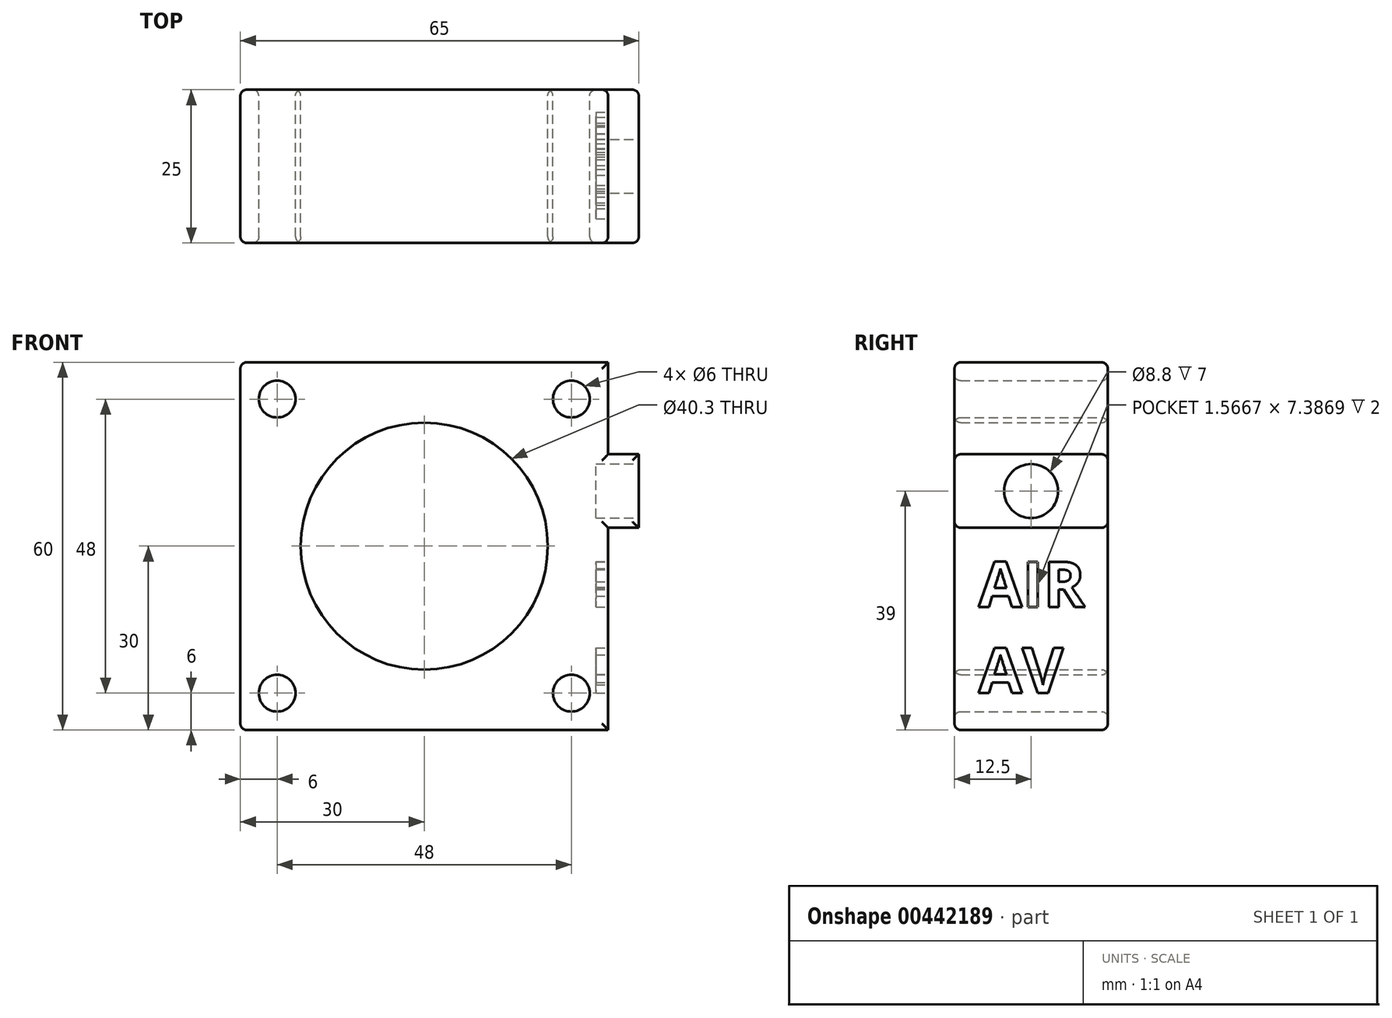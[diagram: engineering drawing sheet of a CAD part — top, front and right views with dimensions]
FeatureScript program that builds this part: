
annotation { "Feature Type Name" : "Feature", "Feature Type Description" : "" }
export const myFeature = defineFeature(function(context is Context, id is Id, definition is map)
    precondition{}
    {
        {
            var Q0;
            Q0=qCreatedBy(makeId("Front.planeOp"),FACE);
            var sketch = newSketch(context, id + "F0", { "sketchPlane" : qUnion([Q0])});
            skCircle(sketch, "E0", {"center": v(0, 0) * mm, "radius": 20.15 * mm});
            skLineSegment(sketch, "E1.bottom", {"start": v(30, -30) * mm, "end": v(-30, -30) * mm});
            skLineSegment(sketch, "E1.top", {"start": v(30, 30) * mm, "end": v(-30, 30) * mm});
            skLineSegment(sketch, "E1.left", {"start": v(30, -30) * mm, "end": v(30, 30) * mm});
            skLineSegment(sketch, "E1.right", {"start": v(-30, -30) * mm, "end": v(-30, 30) * mm});
            skCircle(sketch, "E2", {"center": v(-24, 24) * mm, "radius": 3 * mm});
            skCircle(sketch, "E3", {"center": v(24, 24) * mm, "radius": 3 * mm});
            skCircle(sketch, "E4", {"center": v(24, -24) * mm, "radius": 3 * mm});
            skCircle(sketch, "E5", {"center": v(-24, -24) * mm, "radius": 3 * mm});
            skSolve(sketch);
        }
        {
            var Q0;
            Q0=makeQuery(id+"F0.imprint","IMPRINT",FACE,{"disambiguationData":[TD([[makeQuery(id+"F0.imprint","IMPRINT",EDGE,{"derivedFrom":sQuery(id+"F0.wireOp",EDGE,"E0")}),-1.0]])]});
            extrude(context, id + "F1", {"entities" : qUnion([Q0]), "depth" : 25 * mm});
        }
        {
            var Q0;
            Q0=makeQuery(id+"F1.opExtrude","SWEPT_EDGE",EDGE,{"disambiguationData":[OSD([sQuery(id+"F0.wireOp",EDGE,"E1.top"),sQuery(id+"F0.wireOp",EDGE,"E1.left")])]});
            cPlane(context, id + "F2", {"entities" : qUnion([Q0]), "cplaneType" : CPlaneType.LINE_ANGLE, "offset" : 25 * mm, "angle" : 45 * degree, "width" : 150 * mm, "height" : 150 * mm});
        }
        {
            var Q0;
            Q0=qCreatedBy(id+"F2.planeOp",FACE);
            var sketch = newSketch(context, id + "F3", { "sketchPlane" : qUnion([Q0])});
            skLineSegment(sketch, "E6.bottom", {"start": v(6.06, -5) * mm, "end": v(5.06, -5) * mm});
            skLineSegment(sketch, "E6.top", {"start": v(6.06, -20) * mm, "end": v(5.06, -20) * mm});
            skLineSegment(sketch, "E6.left", {"start": v(7.06, -6) * mm, "end": v(7.06, -19) * mm});
            skLineSegment(sketch, "E6.right", {"start": v(4.06, -6) * mm, "end": v(4.06, -19) * mm});
            skPoint(sketch, "E6.middle", {"position": v(5.56, -12.5) * mm});
            skPoint(sketch, "E7.visualSharp", {"position": v(4.06, -20) * mm});
            skArc(sketch, "E7.filletArc", {"start": v(4.06, -19) * mm, "mid": v(4.36, -19.7) * mm, "end": v(5.06, -20) * mm});
            skPoint(sketch, "E8.visualSharp", {"position": v(4.06, -5) * mm});
            skArc(sketch, "E8.filletArc", {"start": v(5.06, -5) * mm, "mid": v(4.36, -5.3) * mm, "end": v(4.06, -6) * mm});
            skPoint(sketch, "E9.visualSharp", {"position": v(7.06, -5) * mm});
            skArc(sketch, "E9.filletArc", {"start": v(7.06, -6) * mm, "mid": v(6.77, -5.3) * mm, "end": v(6.06, -5) * mm});
            skPoint(sketch, "E10.visualSharp", {"position": v(7.06, -20) * mm});
            skArc(sketch, "E10.filletArc", {"start": v(6.06, -20) * mm, "mid": v(6.77, -19.7) * mm, "end": v(7.06, -19) * mm});
            skSolve(sketch);
        }
        {
            var Q0;
            Q0=qCreatedBy(id+"F2.planeOp",FACE);
            var sketch = newSketch(context, id + "F4", { "sketchPlane" : qUnion([Q0])});
            skLineSegment(sketch, "E11.bottom", {"start": v(16.56, -2.5) * mm, "end": v(13.06, -2.5) * mm});
            skLineSegment(sketch, "E11.top", {"start": v(16.56, -22.5) * mm, "end": v(13.06, -22.5) * mm});
            skLineSegment(sketch, "E11.left", {"start": v(16.56, -2.5) * mm, "end": v(16.56, -22.5) * mm});
            skLineSegment(sketch, "E11.right", {"start": v(13.06, -2.5) * mm, "end": v(13.06, -22.5) * mm});
            skPoint(sketch, "E11.middle", {"position": v(14.81, -12.5) * mm});
            skSolve(sketch);
        }
        {
            var Q0;
            Q0=makeQuery(id+"F4.imprint","IMPRINT",FACE,{"disambiguationData":[TD([[makeQuery(id+"F4.imprint","IMPRINT",EDGE,{"derivedFrom":sQuery(id+"F4.wireOp",EDGE,"E11.bottom")}),1.0]])]});
            extrude(context, id + "F5", {"entities" : qUnion([Q0]), "operationType" : NewBodyOperationType.REMOVE, "oppositeDirection" : true, "depth" : 50 * mm});
        }
        {
            var Q0;
            Q0=makeQuery(id+"F1.opExtrude","SWEPT_FACE",FACE,{"disambiguationData":[OSD([sQuery(id+"F0.wireOp",EDGE,"E1.left")])]});
            var sketch = newSketch(context, id + "F6", { "sketchPlane" : qUnion([Q0])});
            skLineSegment(sketch, "E12.bottom", {"start": v(-25, 15) * mm, "end": v(0, 15) * mm});
            skLineSegment(sketch, "E12.top", {"start": v(-25, 3) * mm, "end": v(0, 3) * mm});
            skLineSegment(sketch, "E12.left", {"start": v(-25, 15) * mm, "end": v(-25, 3) * mm});
            skLineSegment(sketch, "E12.right", {"start": v(0, 15) * mm, "end": v(0, 3) * mm});
            skSolve(sketch);
        }
        {
            var Q0;
            {var subQ0=makeQuery(id+"F1.opExtrude","SWEPT_FACE",FACE,{"disambiguationData":[OSD([sQuery(id+"F0.wireOp",EDGE,"E1.left")])]});Q0=makeQuery(id+"F6.imprint","IMPRINT",FACE,{"disambiguationData":[TD([[makeQuery(id+"F6.imprint","IMPRINT",EDGE,{"derivedFrom":makeQuery(id+"F5.boolean.opBoolean","INTERSECT",EDGE,{"derivedFrom":[subQ0,makeQuery(id+"F5.opExtrude","SWEPT_FACE",FACE,{"disambiguationData":[OSD([sQuery(id+"F4.wireOp",EDGE,"E11.bottom")])]})]})}),-1.0]])]});}
            var Q1;
            Q1=makeQuery(id+"F6.imprint","IMPRINT",FACE,{"disambiguationData":[TD([[makeQuery(id+"F6.imprint","IMPRINT",EDGE,{"derivedFrom":sQuery(id+"F6.wireOp",EDGE,"E12.bottom")}),-1.0]])]});
            extrude(context, id + "F7", {"entities" : qUnion([Q0, Q1]), "operationType" : NewBodyOperationType.ADD, "depth" : 5 * mm});
        }
        {
            var Q0;
            Q0=makeQuery(id+"F7.opExtrude","CAP_FACE",FACE,{"disambiguationData":[OSD([sQuery(id+"F6.wireOp",EDGE,"E12.bottom"),sQuery(id+"F6.wireOp",EDGE,"E12.top"),sQuery(id+"F6.wireOp",EDGE,"E12.left"),sQuery(id+"F6.wireOp",EDGE,"E12.right")])],"isStart":false});
            var sketch = newSketch(context, id + "F8", { "sketchPlane" : qUnion([Q0])});
            skLineSegment(sketch, "E13", {"start": v(-12.5, 15) * mm, "end": v(-12.5, 3) * mm});
            skLineSegment(sketch, "E14", {"start": v(-12.5, 3) * mm, "end": v(-25, 9) * mm});
            skLineSegment(sketch, "E15", {"start": v(-25, 9) * mm, "end": v(0, 9) * mm});
            skCircle(sketch, "E16", {"center": v(-12.5, 9) * mm, "radius": 4.4 * mm});
            skSolve(sketch);
        }
        {
            var Q0;
            {var subQ0=sQuery(id+"F8.wireOp",EDGE,"E15");var subQ1=sQuery(id+"F8.wireOp",EDGE,"E13");var subQ2=makeQuery(id+"F8.imprint","INTERSECT",VERTEX,{"derivedFrom":[subQ1,subQ0]});Q0=makeQuery(id+"F8.imprint","IMPRINT",FACE,{"disambiguationData":[TD([[makeQuery(id+"F8.imprint","IMPRINT",EDGE,{"disambiguationData":[TD([[subQ2,-1.0]])],"derivedFrom":subQ1}),-1.0]])]});}
            var Q1;
            {var subQ0=sQuery(id+"F8.wireOp",EDGE,"E16");var subQ1=sQuery(id+"F8.wireOp",EDGE,"E13");var subQ2=makeQuery(id+"F8.imprint","INTERSECT",VERTEX,{"disambiguationData":[OD(0.0)],"derivedFrom":[subQ1,subQ0]});Q1=makeQuery(id+"F8.imprint","IMPRINT",FACE,{"disambiguationData":[TD([[makeQuery(id+"F8.imprint","IMPRINT",EDGE,{"disambiguationData":[TD([[subQ2,-1.0]])],"derivedFrom":subQ1}),-1.0]])]});}
            var Q2;
            {var subQ0=sQuery(id+"F8.wireOp",EDGE,"E16");var subQ1=sQuery(id+"F8.wireOp",EDGE,"E13");var subQ2=makeQuery(id+"F8.imprint","INTERSECT",VERTEX,{"disambiguationData":[OD(0.0)],"derivedFrom":[subQ1,subQ0]});Q2=makeQuery(id+"F8.imprint","IMPRINT",FACE,{"disambiguationData":[TD([[makeQuery(id+"F8.imprint","IMPRINT",EDGE,{"disambiguationData":[TD([[subQ2,-1.0]])],"derivedFrom":subQ1}),1.0]])]});}
            var Q3;
            {var subQ0=sQuery(id+"F8.wireOp",EDGE,"E15");var subQ1=sQuery(id+"F8.wireOp",EDGE,"E13");var subQ2=makeQuery(id+"F8.imprint","INTERSECT",VERTEX,{"derivedFrom":[subQ1,subQ0]});Q3=makeQuery(id+"F8.imprint","IMPRINT",FACE,{"disambiguationData":[TD([[makeQuery(id+"F8.imprint","IMPRINT",EDGE,{"disambiguationData":[TD([[subQ2,-1.0]])],"derivedFrom":subQ1}),1.0]])]});}
            extrude(context, id + "F9", {"entities" : qUnion([Q0, Q1, Q2, Q3]), "operationType" : NewBodyOperationType.REMOVE, "oppositeDirection" : true, "depth" : 7 * mm});
        }
        {
            var Q0;
            Q0=makeQuery(id+"F1.opExtrude","SWEPT_EDGE",EDGE,{"disambiguationData":[OSD([sQuery(id+"F0.wireOp",EDGE,"E1.top"),sQuery(id+"F0.wireOp",EDGE,"E1.right")])]});
            var Q1;
            Q1=makeQuery(id+"F1.opExtrude","SWEPT_EDGE",EDGE,{"disambiguationData":[OSD([sQuery(id+"F0.wireOp",EDGE,"E1.bottom"),sQuery(id+"F0.wireOp",EDGE,"E1.right")])]});
            var Q2;
            Q2=makeQuery(id+"F1.opExtrude","SWEPT_FACE",FACE,{"disambiguationData":[OSD([sQuery(id+"F0.wireOp",EDGE,"E1.right")])]});
            var Q3;
            Q3=makeQuery(id+"F7.boolean.opBoolean","MERGE",FACE,{"derivedFrom":[makeQuery(id+"F1.opExtrude","CAP_FACE",FACE,{"disambiguationData":[OSD([sQuery(id+"F0.wireOp",EDGE,"E0"),sQuery(id+"F0.wireOp",EDGE,"E1.bottom"),sQuery(id+"F0.wireOp",EDGE,"E1.top"),sQuery(id+"F0.wireOp",EDGE,"E1.left"),sQuery(id+"F0.wireOp",EDGE,"E1.right"),sQuery(id+"F0.wireOp",EDGE,"E2"),sQuery(id+"F0.wireOp",EDGE,"E3"),sQuery(id+"F0.wireOp",EDGE,"E4"),sQuery(id+"F0.wireOp",EDGE,"E5")])],"isStart":true}),makeQuery(id+"F7.opExtrude","SWEPT_FACE",FACE,{"disambiguationData":[OSD([sQuery(id+"F6.wireOp",EDGE,"E12.right")])]})]});
            var Q4;
            Q4=makeQuery(id+"F7.boolean.opBoolean","MERGE",FACE,{"derivedFrom":[makeQuery(id+"F1.opExtrude","CAP_FACE",FACE,{"disambiguationData":[OSD([sQuery(id+"F0.wireOp",EDGE,"E0"),sQuery(id+"F0.wireOp",EDGE,"E1.bottom"),sQuery(id+"F0.wireOp",EDGE,"E1.top"),sQuery(id+"F0.wireOp",EDGE,"E1.left"),sQuery(id+"F0.wireOp",EDGE,"E1.right"),sQuery(id+"F0.wireOp",EDGE,"E2"),sQuery(id+"F0.wireOp",EDGE,"E3"),sQuery(id+"F0.wireOp",EDGE,"E4"),sQuery(id+"F0.wireOp",EDGE,"E5")])],"isStart":false}),makeQuery(id+"F7.opExtrude","SWEPT_FACE",FACE,{"disambiguationData":[OSD([sQuery(id+"F6.wireOp",EDGE,"E12.left")])]})]});
            fillet(context, id + "F10", {"entities" : qUnion([Q0, Q1, Q2, Q3, Q4]), "radius" : 1 * mm, "tangentPropagation" : true, "allowEdgeOverflow" : false});
        }
        {
            var Q0;
            {var subQ0=sQuery(id+"F0.wireOp",EDGE,"E1.bottom");var subQ6=sQuery(id+"F0.wireOp",EDGE,"E1.left");Q0=makeQuery(id+"F7.boolean.opBoolean","SPLIT",FACE,{"disambiguationData":[TD([makeQuery(id+"F1.opExtrude","SWEPT_FACE",FACE,{"disambiguationData":[OSD([subQ0])]})])],"derivedFrom":makeQuery(id+"F1.opExtrude","SWEPT_FACE",FACE,{"disambiguationData":[OSD([subQ6])]})});}
            var sketch = newSketch(context, id + "F11", { "sketchPlane" : qUnion([Q0])});
            skText(sketch, "E17", { "text": "AIR\nAV", "fontName": "OpenSans-Bold.ttf"});
            const initialGuessF11  = {"E17": [-0.02108, -0.00993, 1, 0, 0.00745]};
            skSetInitialGuess(sketch, initialGuessF11);
            skSolve(sketch);
        }
        {
            var Q0;
            Q0 = qSketchRegion(id + "F11", true);
            extrude(context, id + "F12", {"entities" : qUnion([Q0]), "operationType" : NewBodyOperationType.REMOVE, "oppositeDirection" : true, "depth" : 2 * mm});
        }
    });
